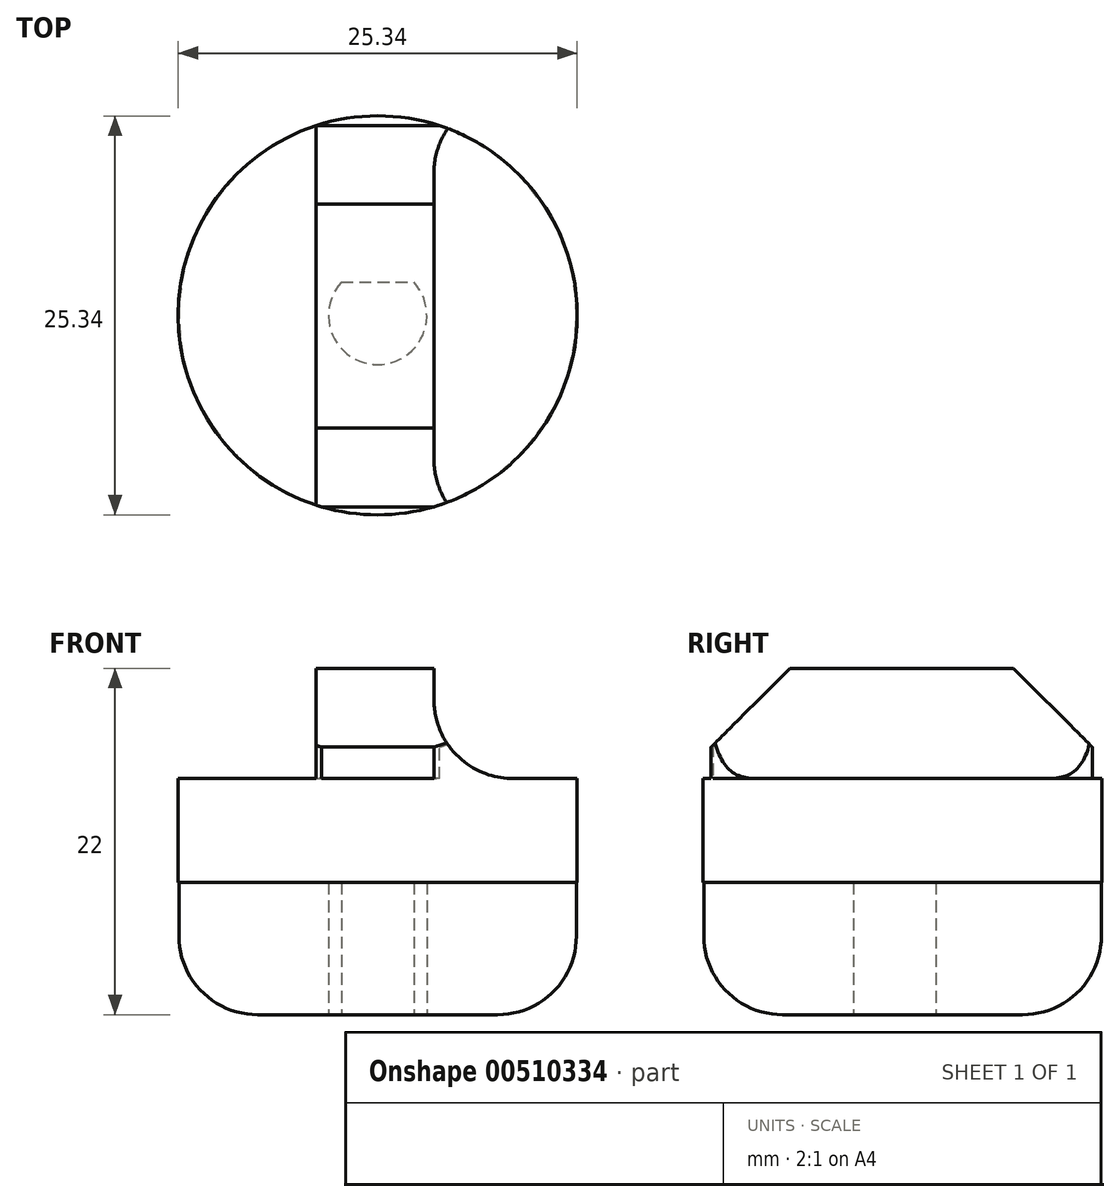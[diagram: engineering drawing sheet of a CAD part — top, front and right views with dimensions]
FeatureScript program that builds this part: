
annotation { "Feature Type Name" : "Feature", "Feature Type Description" : "" }
export const myFeature = defineFeature(function(context is Context, id is Id, definition is map)
    precondition{}
    {
        {
            var Q0;
            Q0=qCreatedBy(makeId("Top.planeOp"),FACE);
            var sketch = newSketch(context, id + "F0", { "sketchPlane" : qUnion([Q0])});
            skCircle(sketch, "E0", {"center": v(0, 0) * mm, "radius": 12.62 * mm});
            skCircle(sketch, "E1.0", {"center": v(0, 0) * mm, "radius": 10.38 * mm});
            skCircle(sketch, "E2", {"center": v(0, 0) * mm, "radius": 5 * mm});
            skCircle(sketch, "E3", {"center": v(0, 0) * mm, "radius": 3.12 * mm});
            skLineSegment(sketch, "E4", {"start": v(-2.3, 2.11) * mm, "end": v(2.3, 2.11) * mm});
            skSolve(sketch);
        }
        {
            var Q0;
            Q0=makeQuery(id+"F0.imprint","IMPRINT",FACE,{"disambiguationData":[TD([[makeQuery(id+"F0.imprint","IMPRINT",EDGE,{"derivedFrom":sQuery(id+"F0.wireOp",EDGE,"E1.0")}),1.0]])]});
            var Q1;
            Q1=makeQuery(id+"F0.imprint","IMPRINT",FACE,{"disambiguationData":[TD([[makeQuery(id+"F0.imprint","IMPRINT",EDGE,{"derivedFrom":sQuery(id+"F0.wireOp",EDGE,"E0")}),1.0]])]});
            extrude(context, id + "F1", {"entities" : qUnion([Q0, Q1]), "depth" : 15 * mm});
        }
        {
            var Q0;
            Q0=makeQuery(id+"F0.imprint","IMPRINT",FACE,{"disambiguationData":[TD([[makeQuery(id+"F0.imprint","IMPRINT",EDGE,{"derivedFrom":sQuery(id+"F0.wireOp",EDGE,"E2")}),1.0]])]});
            var Q1;
            {var subQ0=sQuery(id+"F0.wireOp",EDGE,"kcsZYRUV-fOb9-CoZI-3tOm-9hxGfB4E4ohr");Q1=makeQuery(id+"F0.imprint","IMPRINT",FACE,{"disambiguationData":[TD([[makeQuery(id+"F0.imprint","IMPRINT",EDGE,{"derivedFrom":subQ0}),-1.0]])]});}
            var Q2;
            {var subQ0=sQuery(id+"F0.wireOp",EDGE,"E4");Q2=makeQuery(id+"F0.imprint","IMPRINT",FACE,{"disambiguationData":[TD([[makeQuery(id+"F0.imprint","IMPRINT",EDGE,{"derivedFrom":subQ0}),1.0]])]});}
            extrude(context, id + "F2", {"entities" : qUnion([Q0, Q1, Q2]), "operationType" : NewBodyOperationType.ADD, "depth" : 15 * mm});
        }
        {
            var Q0;
            {var subQ0=sQuery(id+"F0.wireOp",EDGE,"E2");Q0=makeQuery(id+"F2.boolean.opBoolean","MERGE",FACE,{"derivedFrom":[makeQuery(id+"F1.opExtrude","CAP_FACE",FACE,{"disambiguationData":[OSD([sQuery(id+"F0.wireOp",EDGE,"E0"),subQ0])],"isStart":false}),makeQuery(id+"F2.opExtrude","CAP_FACE",FACE,{"disambiguationData":[OSD([subQ0,sQuery(id+"F0.wireOp",EDGE,"E3"),sQuery(id+"F0.wireOp",EDGE,"kcsZYRUV-fOb9-CoZI-3tOm-9hxGfB4E4ohr")])],"isStart":false})]});}
            var sketch = newSketch(context, id + "F3", { "sketchPlane" : qUnion([Q0])});
            skCircle(sketch, "E5", {"center": v(0, 0) * mm, "radius": 12.67 * mm});
            skSolve(sketch);
        }
        {
            var Q0;
            Q0 = qSketchRegion(id + "F3", true);
            extrude(context, id + "F4", {"entities" : qUnion([Q0]), "operationType" : NewBodyOperationType.ADD, "oppositeDirection" : true, "depth" : 6.6 * mm});
        }
        {
            var Q0;
            {var subQ0=sQuery(id+"F0.wireOp",EDGE,"E2");Q0=makeQuery(id+"F4.boolean.opBoolean","MERGE",FACE,{"derivedFrom":[makeQuery(id+"F2.boolean.opBoolean","MERGE",FACE,{"derivedFrom":[makeQuery(id+"F1.opExtrude","CAP_FACE",FACE,{"disambiguationData":[OSD([sQuery(id+"F0.wireOp",EDGE,"E0"),subQ0])],"isStart":false}),makeQuery(id+"F2.opExtrude","CAP_FACE",FACE,{"disambiguationData":[OSD([subQ0,sQuery(id+"F0.wireOp",EDGE,"E3"),sQuery(id+"F0.wireOp",EDGE,"kcsZYRUV-fOb9-CoZI-3tOm-9hxGfB4E4ohr")])],"isStart":false})]}),makeQuery(id+"F4.opExtrude","CAP_FACE",FACE,{"disambiguationData":[OSD([sQuery(id+"F3.wireOp",EDGE,"E5")])],"isStart":true})]});}
            var sketch = newSketch(context, id + "F5", { "sketchPlane" : qUnion([Q0])});
            skLineSegment(sketch, "E6.bottom", {"start": v(-3.92, 12.05) * mm, "end": v(3.58, 12.05) * mm});
            skLineSegment(sketch, "E6.top", {"start": v(-3.92, -12.16) * mm, "end": v(3.58, -12.16) * mm});
            skLineSegment(sketch, "E6.left", {"start": v(-3.92, 12.05) * mm, "end": v(-3.92, -12.16) * mm});
            skLineSegment(sketch, "E6.right", {"start": v(3.58, 12.05) * mm, "end": v(3.58, -12.16) * mm});
            skSolve(sketch);
        }
        {
            var Q0;
            {var subQ1=sQuery(id+"F5.wireOp",EDGE,"E6.bottom");Q0=makeQuery(id+"F5.imprint","IMPRINT",FACE,{"disambiguationData":[TD([[makeQuery(id+"F5.imprint","IMPRINT",EDGE,{"derivedFrom":subQ1}),-1.0]])]});}
            extrude(context, id + "F6", {"entities" : qUnion([Q0]), "operationType" : NewBodyOperationType.ADD, "depth" : 7 * mm});
        }
        {
            var Q0;
            Q0=makeQuery(id+"F6.opExtrude","CAP_EDGE",EDGE,{"disambiguationData":[OSD([sQuery(id+"F5.wireOp",EDGE,"E6.left")])],"isStart":true});
            var Q1;
            Q1=makeQuery(id+"F6.opExtrude","CAP_EDGE",EDGE,{"disambiguationData":[OSD([sQuery(id+"F5.wireOp",EDGE,"E6.right")])],"isStart":true});
            fillet(context, id + "F7", {"entities" : qUnion([Q0, Q1]), "radius" : 5 * mm, "tangentPropagation" : true, "allowEdgeOverflow" : false});
        }
        {
            var Q0;
            Q0=makeQuery(id+"F6.opExtrude","CAP_EDGE",EDGE,{"disambiguationData":[OSD([sQuery(id+"F5.wireOp",EDGE,"E6.top")])],"isStart":false});
            chamfer(context, id + "F8", {"entities" : qUnion([Q0]), "width" : 5 * mm, "tangentPropagation" : true});
        }
        {
            var Q0;
            Q0=makeQuery(id+"F6.opExtrude","CAP_EDGE",EDGE,{"disambiguationData":[OSD([sQuery(id+"F5.wireOp",EDGE,"E6.bottom")])],"isStart":false});
            chamfer(context, id + "F9", {"entities" : qUnion([Q0]), "width" : 5 * mm, "tangentPropagation" : true});
        }
        {
            var Q0;
            Q0=makeQuery(id+"F1.opExtrude","CAP_EDGE",EDGE,{"disambiguationData":[OSD([sQuery(id+"F0.wireOp",EDGE,"E0")])],"isStart":true});
            fillet(context, id + "F10", {"entities" : qUnion([Q0]), "radius" : 5 * mm, "tangentPropagation" : true, "allowEdgeOverflow" : false});
        }
    });
